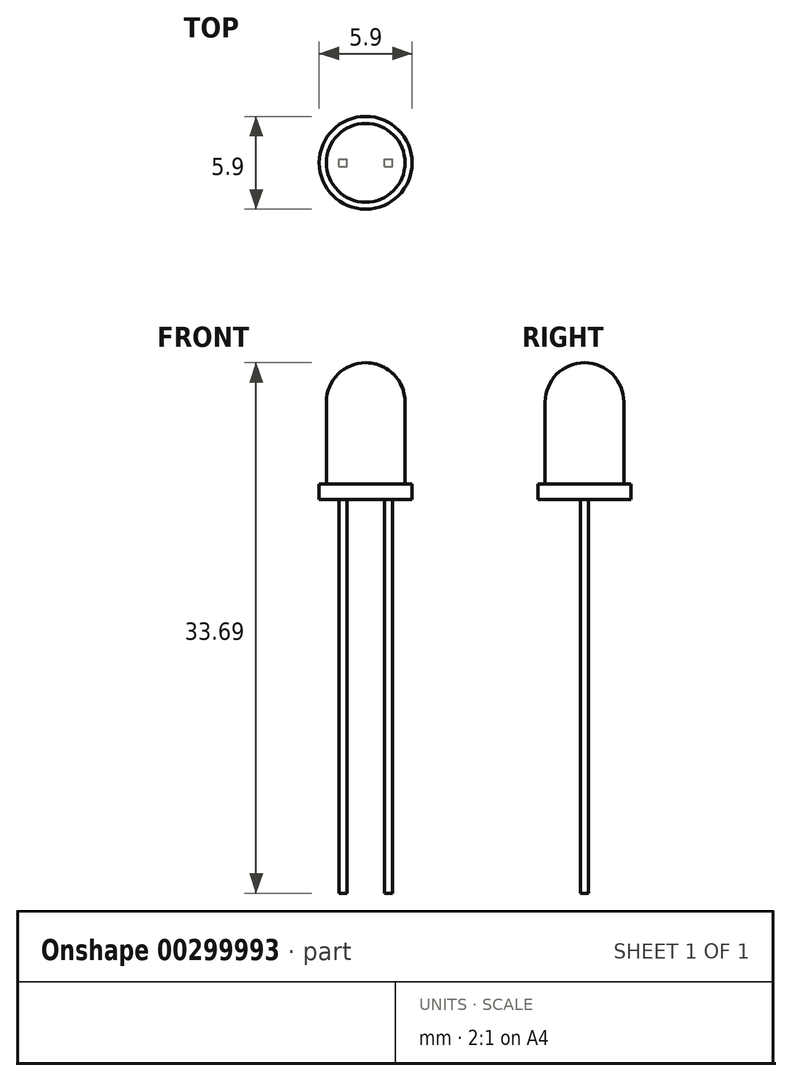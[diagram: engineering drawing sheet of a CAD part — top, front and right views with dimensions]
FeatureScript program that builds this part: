
annotation { "Feature Type Name" : "Feature", "Feature Type Description" : "" }
export const myFeature = defineFeature(function(context is Context, id is Id, definition is map)
    precondition{}
    {
        {
            var Q0;
            Q0=qCreatedBy(makeId("Front.planeOp"),FACE);
            var sketch = newSketch(context, id + "F0", { "sketchPlane" : qUnion([Q0])});
            skLineSegment(sketch, "E0", {"start": v(0, 0) * mm, "end": v(0, 6.19) * mm});
            skArc(sketch, "E1", {"start": v(0, 3.69) * mm, "mid": v(2.5, 6.19) * mm, "end": v(0, 8.7) * mm});
            skLineSegment(sketch, "E2", {"start": v(0, 0) * mm, "end": v(2.95, 0) * mm});
            skLineSegment(sketch, "E3", {"start": v(0, 6.19) * mm, "end": v(2.5, 6.19) * mm});
            skLineSegment(sketch, "E4", {"start": v(2.5, 6.19) * mm, "end": v(2.5, 0) * mm});
            skLineSegment(sketch, "E5", {"start": v(2.95, 0) * mm, "end": v(2.95, 1) * mm});
            skLineSegment(sketch, "E6", {"start": v(2.95, 1) * mm, "end": v(0, 1) * mm});
            skLineSegment(sketch, "E7", {"start": v(0, 6.19) * mm, "end": v(0, 8.7) * mm});
            skSolve(sketch);
        }
        {
            var Q0;
            Q0 = qSketchRegion(id + "F0", true);
            var Q1;
            Q1=sQuery(id+"F0.wireOp",EDGE,"E0");
            revolve(context, id + "F1", {"entities" : qUnion([Q0]), "axis" : qUnion([Q1]), "revolveType" : RevolveType.FULL});
        }
        {
            var Q0;
            Q0=makeQuery(id+"F1.opRevolve","SWEPT_FACE",FACE,{"disambiguationData":[OSD([sQuery(id+"F0.wireOp",EDGE,"E2")])]});
            var sketch = newSketch(context, id + "F2", { "sketchPlane" : qUnion([Q0])});
            skLineSegment(sketch, "E8.bottom", {"start": v(-1.7, 0.25) * mm, "end": v(-1.2, 0.25) * mm});
            skLineSegment(sketch, "E8.top", {"start": v(-1.7, -0.25) * mm, "end": v(-1.2, -0.25) * mm});
            skLineSegment(sketch, "E8.left", {"start": v(-1.7, 0.25) * mm, "end": v(-1.7, -0.25) * mm});
            skLineSegment(sketch, "E8.right", {"start": v(-1.2, 0.25) * mm, "end": v(-1.2, -0.25) * mm});
            skLineSegment(sketch, "E9.bottom", {"start": v(1.2, 0.25) * mm, "end": v(1.7, 0.25) * mm});
            skLineSegment(sketch, "E9.top", {"start": v(1.2, -0.25) * mm, "end": v(1.7, -0.25) * mm});
            skLineSegment(sketch, "E9.left", {"start": v(1.2, 0.25) * mm, "end": v(1.2, -0.25) * mm});
            skLineSegment(sketch, "E9.right", {"start": v(1.7, 0.25) * mm, "end": v(1.7, -0.25) * mm});
            skSolve(sketch);
        }
        {
            var Q0;
            Q0 = qSketchRegion(id + "F2", true);
            extrude(context, id + "F3", {"entities" : qUnion([Q0]), "operationType" : NewBodyOperationType.ADD, "depth" : 25 * mm});
        }
    });
